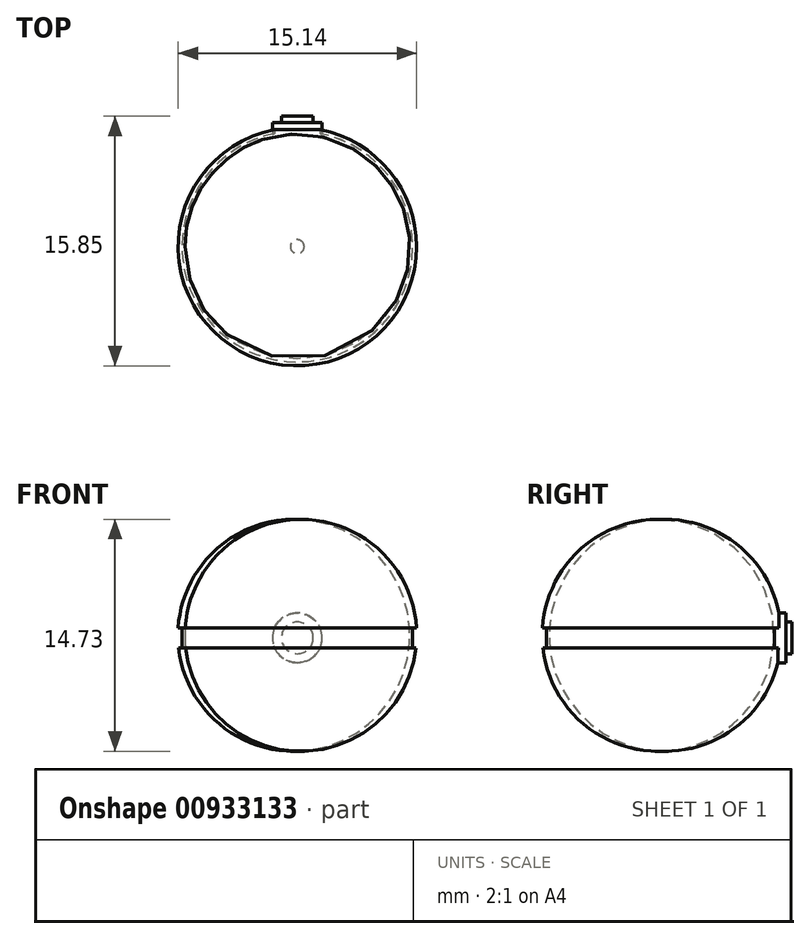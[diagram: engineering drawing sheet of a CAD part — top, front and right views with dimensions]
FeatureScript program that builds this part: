
annotation { "Feature Type Name" : "Feature", "Feature Type Description" : "" }
export const myFeature = defineFeature(function(context is Context, id is Id, definition is map)
    precondition{}
    {
        {
            var Q0;
            Q0=qCreatedBy(makeId("Front.planeOp"),FACE);
            var sketch = newSketch(context, id + "F0", { "sketchPlane" : qUnion([Q0])});
            skLineSegment(sketch, "E0", {"start": v(0, 73.44) * mm, "end": v(0, -78.53) * mm});
            skArc(sketch, "E1", {"start": v(0, 7.52) * mm, "mid": v(-7.59, 0.16) * mm, "end": v(0, -7.2) * mm});
            skLineSegment(sketch, "E2.bottom", {"start": v(-7.54, -0.65) * mm, "end": v(-7.33, -0.65) * mm});
            skLineSegment(sketch, "E2.top", {"start": v(-7.54, 0.63) * mm, "end": v(-7.33, 0.63) * mm});
            skLineSegment(sketch, "E2.right", {"start": v(-7.33, -0.65) * mm, "end": v(-7.33, 0.63) * mm});
            skLineSegment(sketch, "E3", {"start": v(-7.54, 0.63) * mm, "end": v(-7.57, 0.63) * mm});
            skSolve(sketch);
        }
        {
            var Q0;
            {var subQ0=sQuery(id+"F0.wireOp",EDGE,"E2.bottom");Q0=makeQuery(id+"F0.imprint","IMPRINT",FACE,{"disambiguationData":[TD([[makeQuery(id+"F0.imprint","IMPRINT",EDGE,{"derivedFrom":subQ0}),-1.0]])]});}
            var Q1;
            Q1=sQuery(id+"F0.wireOp",EDGE,"E0");
            revolve(context, id + "F1", {"surfaceOperationType" : NewSurfaceOperationType.NEW, "entities" : qUnion([Q0]), "axis" : qUnion([Q1]), "revolveType" : RevolveType.FULL});
        }
        {
            var Q0;
            Q0=qCreatedBy(makeId("Front.planeOp"),FACE);
            var sketch = newSketch(context, id + "F2", { "sketchPlane" : qUnion([Q0])});
            skCircle(sketch, "E4", {"center": v(0, 0) * mm, "radius": 1.58 * mm});
            skSolve(sketch);
        }
        {
            var Q0;
            Q0=makeQuery(id+"F2.imprint","IMPRINT",FACE,{"disambiguationData":[TD([[makeQuery(id+"F2.imprint","IMPRINT",EDGE,{"derivedFrom":sQuery(id+"F2.wireOp",EDGE,"E4")}),1.0]])]});
            extrude(context, id + "F3", {"entities" : qUnion([Q0]), "oppositeDirection" : true, "depth" : 7.88 * mm, "offsetDistance" : 25.4 * mm});
        }
        {
            var Q0;
            Q0=qCreatedBy(makeId("Front.planeOp"),FACE);
            var sketch = newSketch(context, id + "F4", { "sketchPlane" : qUnion([Q0])});
            skCircle(sketch, "E5", {"center": v(0, 0) * mm, "radius": 1 * mm});
            skSolve(sketch);
        }
        {
            var Q0;
            Q0 = qSketchRegion(id + "F4", true);
            var Q1;
            Q1=makeQuery(id+"F4.imprint","IMPRINT",FACE,{"disambiguationData":[TD([[makeQuery(id+"F4.imprint","IMPRINT",EDGE,{"derivedFrom":sQuery(id+"F4.wireOp",EDGE,"E5")}),1.0]])]});
            extrude(context, id + "F5", {"entities" : qUnion([Q0, Q1]), "operationType" : NewBodyOperationType.ADD, "oppositeDirection" : true, "depth" : 8.28 * mm, "offsetDistance" : 25.4 * mm});
        }
    });
